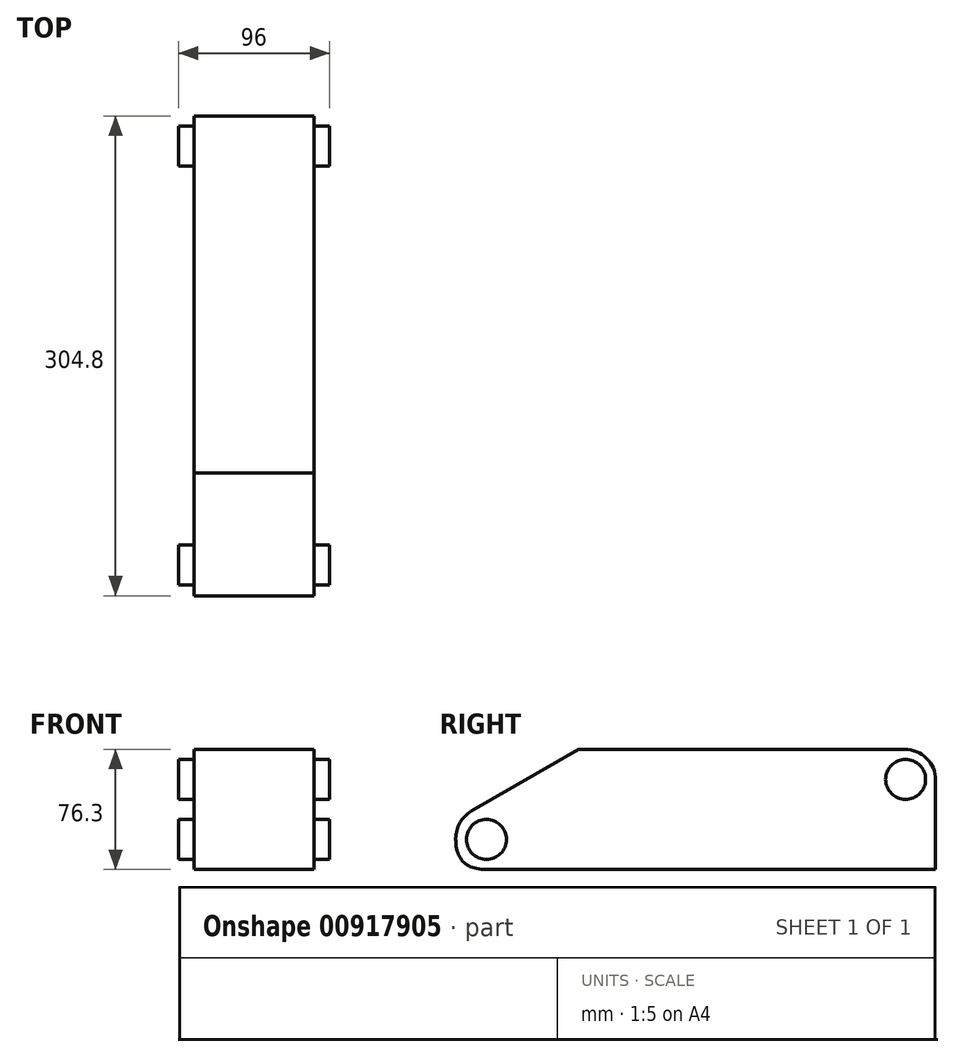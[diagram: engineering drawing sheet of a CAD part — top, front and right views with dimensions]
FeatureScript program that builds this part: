
annotation { "Feature Type Name" : "Feature", "Feature Type Description" : "" }
export const myFeature = defineFeature(function(context is Context, id is Id, definition is map)
    precondition{}
    {
        {
            var Q0;
            Q0=qCreatedBy(makeId("Right.planeOp"),FACE);
            var sketch = newSketch(context, id + "F0", { "sketchPlane" : qUnion([Q0])});
            skLineSegment(sketch, "E0.bottom", {"start": v(0, 0) * mm, "end": v(304.8, 0) * mm});
            skLineSegment(sketch, "E0.top", {"start": v(0, 76.3) * mm, "end": v(304.8, 76.3) * mm});
            skLineSegment(sketch, "E0.left", {"start": v(0, 0) * mm, "end": v(0, 76.3) * mm});
            skLineSegment(sketch, "E0.right", {"start": v(304.8, 0) * mm, "end": v(304.8, 76.3) * mm});
            skSolve(sketch);
        }
        {
            var Q0;
            Q0 = qSketchRegion(id + "F0", true);
            extrude(context, id + "F1", {"entities" : qUnion([Q0]), "depth" : 3 * mm, "offsetDistance" : 25 * mm});
        }
        {
            var Q0;
            Q0 = qSketchRegion(id + "F0", true);
            extrude(context, id + "F2", {"entities" : qUnion([Q0]), "operationType" : NewBodyOperationType.ADD, "depth" : 76.2 * mm, "offsetDistance" : 25 * mm});
        }
        {
            var Q0;
            {var subQ0=sQuery(id+"F0.wireOp",EDGE,"E0.left");var subQ1=sQuery(id+"F0.wireOp",EDGE,"E0.bottom");Q0=makeQuery(id+"F2.boolean.opBoolean","MERGE",EDGE,{"derivedFrom":[makeQuery(id+"F1.opExtrude","SWEPT_EDGE",EDGE,{"disambiguationData":[OSD([subQ1,subQ0])]}),makeQuery(id+"F2.opExtrude","SWEPT_EDGE",EDGE,{"disambiguationData":[OSD([subQ1,subQ0])]})]});}
            fillet(context, id + "F3", {"entities" : qUnion([Q0]), "radius" : 19.5 * mm, "tangentPropagation" : true, "rho" : 0.5, "crossSection" : FilletCrossSection.CONIC, "allowEdgeOverflow" : false});
        }
        {
            var Q0;
            {var subQ0=sQuery(id+"F0.wireOp",EDGE,"E0.right");var subQ1=sQuery(id+"F0.wireOp",EDGE,"E0.top");Q0=makeQuery(id+"F2.boolean.opBoolean","MERGE",EDGE,{"derivedFrom":[makeQuery(id+"F1.opExtrude","SWEPT_EDGE",EDGE,{"disambiguationData":[OSD([subQ1,subQ0])]}),makeQuery(id+"F2.opExtrude","SWEPT_EDGE",EDGE,{"disambiguationData":[OSD([subQ1,subQ0])]})]});}
            fillet(context, id + "F4", {"entities" : qUnion([Q0]), "radius" : 19.5 * mm, "tangentPropagation" : true, "allowEdgeOverflow" : false});
        }
        {
            var Q0;
            {var subQ0=sQuery(id+"F0.wireOp",EDGE,"E0.left");var subQ1=sQuery(id+"F0.wireOp",EDGE,"E0.top");Q0=makeQuery(id+"F2.boolean.opBoolean","MERGE",EDGE,{"derivedFrom":[makeQuery(id+"F1.opExtrude","SWEPT_EDGE",EDGE,{"disambiguationData":[OSD([subQ1,subQ0])]}),makeQuery(id+"F2.opExtrude","SWEPT_EDGE",EDGE,{"disambiguationData":[OSD([subQ1,subQ0])]})]});}
            chamfer(context, id + "F5", {"entities" : qUnion([Q0]), "chamferType" : ChamferType.OFFSET_ANGLE, "width" : 45 * mm, "oppositeDirection" : false, "angle" : 60 * degree, "tangentPropagation" : true});
        }
        {
            var Q0;
            {var subQ0=sQuery(id+"F0.wireOp",EDGE,"E0.left");var subQ1=sQuery(id+"F0.wireOp",EDGE,"E0.top");Q0=makeQuery(id+"F5.opChamfer","BLEND_EDGE",EDGE,{"blendedFrom":[makeQuery(id+"F2.boolean.opBoolean","MERGE",EDGE,{"derivedFrom":[makeQuery(id+"F1.opExtrude","SWEPT_EDGE",EDGE,{"disambiguationData":[OSD([subQ1,subQ0])]}),makeQuery(id+"F2.opExtrude","SWEPT_EDGE",EDGE,{"disambiguationData":[OSD([subQ1,subQ0])]})]}),makeQuery(id+"F2.boolean.opBoolean","MERGE",FACE,{"derivedFrom":[makeQuery(id+"F1.opExtrude","SWEPT_FACE",FACE,{"disambiguationData":[OSD([subQ0])]}),makeQuery(id+"F2.opExtrude","SWEPT_FACE",FACE,{"disambiguationData":[OSD([subQ0])]})]})],"blendedInto":[makeQuery(id+"F2.boolean.opBoolean","MERGE",FACE,{"derivedFrom":[makeQuery(id+"F1.opExtrude","SWEPT_FACE",FACE,{"disambiguationData":[OSD([subQ0])]}),makeQuery(id+"F2.opExtrude","SWEPT_FACE",FACE,{"disambiguationData":[OSD([subQ0])]})]})]});}
            fillet(context, id + "F6", {"entities" : qUnion([Q0]), "radius" : 20.04 * mm, "tangentPropagation" : true, "allowEdgeOverflow" : false});
        }
        {
            var Q0;
            Q0=makeQuery(id+"F2.opExtrude","CAP_FACE",FACE,{"disambiguationData":[OSD([sQuery(id+"F0.wireOp",EDGE,"E0.bottom"),sQuery(id+"F0.wireOp",EDGE,"E0.top"),sQuery(id+"F0.wireOp",EDGE,"E0.left"),sQuery(id+"F0.wireOp",EDGE,"E0.right")])],"isStart":false});
            cPlane(context, id + "F7", {"entities" : qUnion([Q0]), "cplaneType" : CPlaneType.OFFSET, "offset" : 0 * mm, "width" : 150 * mm, "height" : 150 * mm});
        }
        {
            var Q0;
            Q0=qCreatedBy(id+"F7.planeOp",FACE);
            var sketch = newSketch(context, id + "F8", { "sketchPlane" : qUnion([Q0])});
            skCircle(sketch, "E1", {"center": v(19.49, 19.05) * mm, "radius": 12.7 * mm});
            skSolve(sketch);
        }
        {
            var Q0;
            Q0 = qSketchRegion(id + "F8", true);
            extrude(context, id + "F9", {"entities" : qUnion([Q0]), "operationType" : NewBodyOperationType.ADD, "depth" : 10 * mm, "offsetDistance" : 25 * mm, "hasSecondDirection" : true, "secondDirectionOppositeDirection" : true, "secondDirectionDepth" : 86 * mm});
        }
        {
            var Q0;
            Q0=qCreatedBy(id+"F7.planeOp",FACE);
            var sketch = newSketch(context, id + "F10", { "sketchPlane" : qUnion([Q0])});
            skCircle(sketch, "E2", {"center": v(285.75, 57.25) * mm, "radius": 12.7 * mm});
            skSolve(sketch);
        }
        {
            var Q0;
            Q0=makeQuery(id+"F10.imprint","IMPRINT",FACE,{"disambiguationData":[TD([[makeQuery(id+"F10.imprint","IMPRINT",EDGE,{"derivedFrom":sQuery(id+"F10.wireOp",EDGE,"E2")}),1.0]])]});
            extrude(context, id + "F11", {"entities" : qUnion([Q0]), "operationType" : NewBodyOperationType.ADD, "depth" : 10 * mm, "offsetDistance" : 25 * mm, "hasSecondDirection" : true, "secondDirectionOppositeDirection" : true, "secondDirectionDepth" : 86 * mm});
        }
    });
